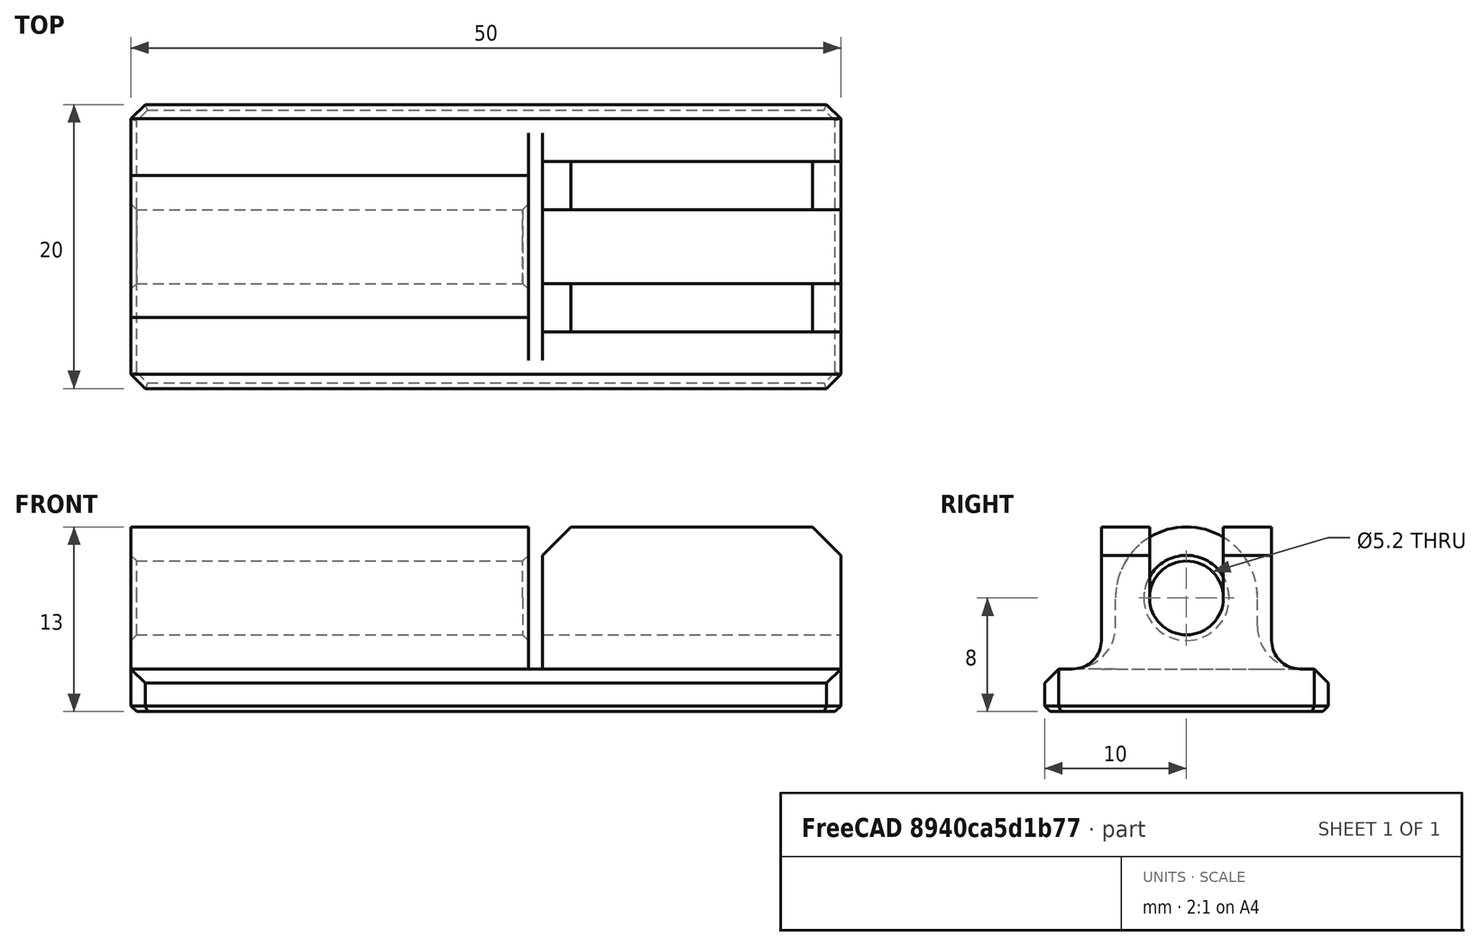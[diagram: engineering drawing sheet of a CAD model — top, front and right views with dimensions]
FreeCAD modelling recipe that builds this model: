
FCSTD DOCUMENT  (FreeCAD 0.18R16146 (Git))
Label: cf-rod-cut-template
License: All rights reserved
LicenseURL: http://en.wikipedia.org/wiki/All_rights_reserved
objects: Part::Box×4, Part::MultiFuse×4, Part::Chamfer×4, Part::Cylinder×3, Part::Fillet×2, Part::Cut×2
note: 19 computed .brp shape members not serialized (recipe doc carries the construction recipe); baked Part::Feature solids carry a one-line shape summary decoded from their .brp

FEATURE [Part::Cylinder] Cylinder
  Angle = 360
  AttacherType = Attacher::AttachEngine3D
  Height = 50
  Placement = pos=(-1.1e-15,0,5) rot=(0,1,0;1.5708rad)
  Radius = 2.6
FEATURE [Part::Box] Box  label="Cube"
  AttacherType = Attacher::AttachEngine3D
  Height = 5
  Length = 28
  Placement = pos=(0,-5,0) rot=(0,0,1;0rad)
  Width = 10
FEATURE [Part::Cylinder] Cylinder001
  Angle = 360
  AttacherType = Attacher::AttachEngine3D
  Height = 28
  Placement = pos=(-1.1e-15,0,5) rot=(0,1,0;1.5708rad)
  Radius = 5
FEATURE [Part::Box] Box001  label="Cube001"
  AttacherType = Attacher::AttachEngine3D
  Height = 3
  Length = 50
  Placement = pos=(0,-10,-3) rot=(0,0,1;0rad)
  Width = 20
FEATURE [Part::MultiFuse] Fusion
  Shapes = -> [Box,Box001]
FEATURE [Part::Fillet] Fillet
  Base = -> Fusion
  Edges = 2 edges r=3: [Edge10,Edge12]
FEATURE [Part::Box] Box002  label="Cube002"
  AttacherType = Attacher::AttachEngine3D
  Height = 10
  Length = 21
  Placement = pos=(29,-6,0) rot=(0,0,1;0rad)
  Width = 12
FEATURE [Part::Box] Box003  label="Cube003"
  AttacherType = Attacher::AttachEngine3D
  Height = 10
  Length = 21
  Placement = pos=(29,-2.6,5) rot=(0,0,1;0rad)
  Width = 5.2
FEATURE [Part::MultiFuse] Fusion001
  Shapes = -> [Cylinder001,Fillet]
FEATURE [Part::Cylinder] Cylinder002
  Angle = 360
  AttacherType = Attacher::AttachEngine3D
  Height = 50
  Placement = pos=(-1.1e-15,0,5) rot=(0,1,0;1.5708rad)
  Radius = 2.6
FEATURE [Part::Cut] Cut
  Base = -> Fusion001
  Tool = -> Cylinder
FEATURE [Part::MultiFuse] Fusion002
  Shapes = -> [Box003,Cylinder002]
FEATURE [Part::Cut] Cut001
  Base = -> Box002
  Tool = -> Fusion002
FEATURE [Part::MultiFuse] Fusion003
  Shapes = -> [Cut001,Cut]
FEATURE [Part::Fillet] Fillet001
  Base = -> Fusion003
  Edges = 2 edges r=2: [Edge47,Edge49]
FEATURE [Part::Chamfer] Chamfer
  Base = -> Fillet001
  Edges = 4 edges r=2: [Edge30,Edge37,Edge58,Edge64]
FEATURE [Part::Chamfer] Chamfer001
  Base = -> Chamfer
  Edges = 6 edges r=1: [Edge28,Edge36,Edge61,Edge63,Edge65,Edge67]
FEATURE [Part::Chamfer] Chamfer002
  Base = -> Chamfer001
  Edges = 8 edges r=0.4: [Edge20,Edge32,Edge61,Edge71,Edge72,Edge73,Edge74,Edge75]
FEATURE [Part::Chamfer] Chamfer003
  Base = -> Chamfer002
  Edges = 6 edges r=0.4: [Edge120,Edge121,Edge125,Edge126,Edge130,Edge132]
